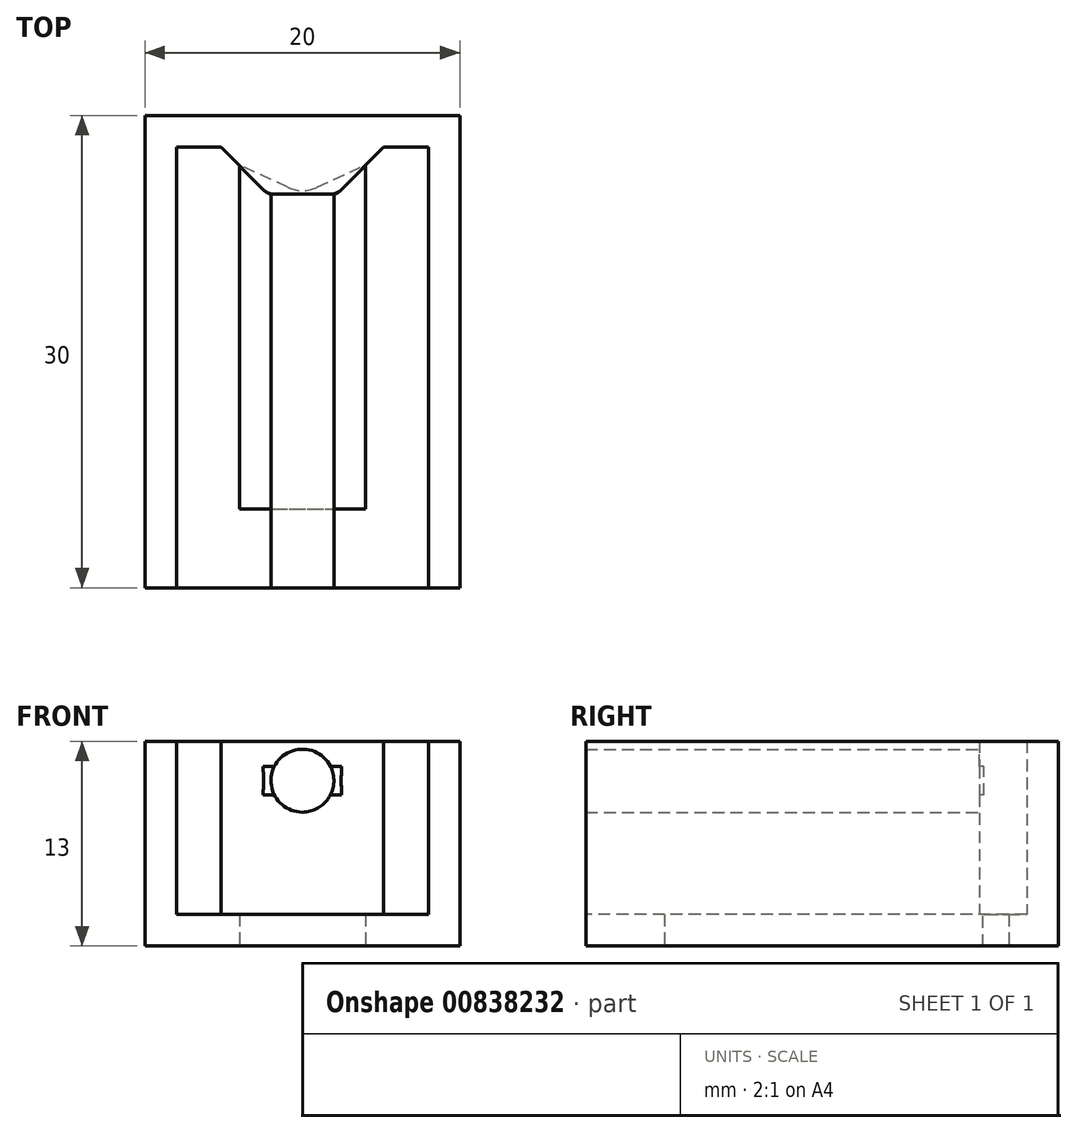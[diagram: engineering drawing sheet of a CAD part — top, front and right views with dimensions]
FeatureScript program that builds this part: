
annotation { "Feature Type Name" : "Feature", "Feature Type Description" : "" }
export const myFeature = defineFeature(function(context is Context, id is Id, definition is map)
    precondition{}
    {
        {
            var Q0;
            Q0=qCreatedBy(makeId("Top.planeOp"),FACE);
            var sketch = newSketch(context, id + "F0", { "sketchPlane" : qUnion([Q0])});
            skLineSegment(sketch, "E0.right", {"start": v(-10, 15) * mm, "end": v(-10, -15) * mm});
            skPoint(sketch, "E0.middle", {"position": v(0, 0) * mm});
            skLineSegment(sketch, "E1", {"start": v(0, 10) * mm, "end": v(-4, 11.86) * mm});
            skLineSegment(sketch, "E2.MirrorCS", {"start": v(10, 15) * mm, "end": v(10, -15) * mm});
            skLineSegment(sketch, "E3.MirrorCS", {"start": v(0, 10) * mm, "end": v(4, 11.86) * mm});
            skLineSegment(sketch, "E4.trimOffspring", {"start": v(-4, -10) * mm, "end": v(4, -10) * mm});
            skLineSegment(sketch, "E5", {"start": v(-4, 11.86) * mm, "end": v(-4, -10) * mm});
            skLineSegment(sketch, "E6", {"start": v(4, 11.86) * mm, "end": v(4, -10) * mm});
            skLineSegment(sketch, "E7", {"start": v(-10, -15) * mm, "end": v(10, -15) * mm});
            skLineSegment(sketch, "E8", {"start": v(-10, 15) * mm, "end": v(10, 15) * mm});
            skSolve(sketch);
        }
        {
            var Q0;
            Q0=makeQuery(id+"F0.imprint","IMPRINT",FACE,{"disambiguationData":[TD([[makeQuery(id+"F0.imprint","IMPRINT",EDGE,{"derivedFrom":sQuery(id+"F0.wireOp",EDGE,"E0.right")}),1.0]])]});
            extrude(context, id + "F1", {"entities" : qUnion([Q0]), "depth" : 2 * mm, "offsetDistance" : 25 * mm});
        }
        {
            var Q0;
            Q0=makeQuery(id+"F1.opExtrude","CAP_FACE",FACE,{"disambiguationData":[OSD([sQuery(id+"F0.wireOp",EDGE,"E0.right"),sQuery(id+"F0.wireOp",EDGE,"yTbLrUah-Ia5R-yqaf-Bvvm-QQtAT4T50mUZ"),sQuery(id+"F0.wireOp",EDGE,"NDNi7f39-i3bd-ZvMG-hIc7-ptrDR7INLeRJ"),sQuery(id+"F0.wireOp",EDGE,"E1"),sQuery(id+"F0.wireOp",EDGE,"E2.MirrorCS"),sQuery(id+"F0.wireOp",EDGE,"4e7f6cf4-dfac-4857-8eba-5604ad7142842.MirrorCS"),sQuery(id+"F0.wireOp",EDGE,"E3.MirrorCS"),sQuery(id+"F0.wireOp",EDGE,"4e7f6cf4-dfac-4857-8eba-5604ad7142845.MirrorCS"),sQuery(id+"F0.wireOp",EDGE,"E4.trimOffspring"),sQuery(id+"F0.wireOp",EDGE,"E5"),sQuery(id+"F0.wireOp",EDGE,"E6"),sQuery(id+"F0.wireOp",EDGE,"E7")])],"isStart":false});
            var sketch = newSketch(context, id + "F2", { "sketchPlane" : qUnion([Q0])});
            skLineSegment(sketch, "E9", {"start": v(0, 10) * mm, "end": v(-2.2, 10) * mm});
            skLineSegment(sketch, "E10", {"start": v(-2.2, 10) * mm, "end": v(-5.16, 13) * mm});
            skLineSegment(sketch, "E11", {"start": v(-5.16, 13) * mm, "end": v(-8, 13) * mm});
            skLineSegment(sketch, "E12", {"start": v(-8, 13) * mm, "end": v(-8, -15) * mm});
            skLineSegment(sketch, "E13", {"start": v(-8, -15) * mm, "end": v(-10, -15) * mm});
            skLineSegment(sketch, "E14", {"start": v(-10, -15) * mm, "end": v(-10, 15) * mm});
            skLineSegment(sketch, "E15.MirrorCS", {"start": v(0, 10) * mm, "end": v(2.2, 10) * mm});
            skLineSegment(sketch, "E16.MirrorCS", {"start": v(2.2, 10) * mm, "end": v(5.16, 13) * mm});
            skLineSegment(sketch, "E17.MirrorCS", {"start": v(5.16, 13) * mm, "end": v(8, 13) * mm});
            skLineSegment(sketch, "E18.MirrorCS", {"start": v(8, 13) * mm, "end": v(8, -15) * mm});
            skLineSegment(sketch, "E19.MirrorCS", {"start": v(8, -15) * mm, "end": v(10, -15) * mm});
            skLineSegment(sketch, "E20.MirrorCS", {"start": v(10, -15) * mm, "end": v(10, 15) * mm});
            skLineSegment(sketch, "E21", {"start": v(-10, 15) * mm, "end": v(10, 15) * mm});
            skSolve(sketch);
        }
        {
            var Q0;
            Q0 = qSketchRegion(id + "F2", true);
            extrude(context, id + "F3", {"entities" : qUnion([Q0]), "operationType" : NewBodyOperationType.ADD, "depth" : 11 * mm, "offsetDistance" : 25 * mm});
        }
        {
            var Q0;
            Q0=makeQuery(id+"F3.opExtrude","SWEPT_FACE",FACE,{"disambiguationData":[OSD([sQuery(id+"F2.wireOp",EDGE,"E9"),sQuery(id+"F2.wireOp",EDGE,"E15.MirrorCS")])]});
            var sketch = newSketch(context, id + "F4", { "sketchPlane" : qUnion([Q0])});
            skCircle(sketch, "E22", {"center": v(0, 10.5) * mm, "radius": 2 * mm});
            skPoint(sketch, "E22.centerSnap0", {"position": v(0, 13) * mm});
            skSolve(sketch);
        }
        {
            var Q0;
            Q0=makeQuery(id+"F4.imprint","IMPRINT",FACE,{"disambiguationData":[TD([[makeQuery(id+"F4.imprint","IMPRINT",EDGE,{"derivedFrom":sQuery(id+"F4.wireOp",EDGE,"E22")}),1.0]])]});
            extrude(context, id + "F5", {"entities" : qUnion([Q0]), "operationType" : NewBodyOperationType.ADD, "depth" : 25 * mm, "offsetDistance" : 25 * mm});
        }
        {
            var Q0;
            Q0=makeQuery(id+"F3.opExtrude","SWEPT_EDGE",EDGE,{"disambiguationData":[OSD([sQuery(id+"F2.wireOp",EDGE,"E15.MirrorCS"),sQuery(id+"F2.wireOp",EDGE,"E16.MirrorCS")])]});
            var Q1;
            Q1=makeQuery(id+"F3.opExtrude","SWEPT_EDGE",EDGE,{"disambiguationData":[OSD([sQuery(id+"F2.wireOp",EDGE,"E9"),sQuery(id+"F2.wireOp",EDGE,"E10")])]});
            fillet(context, id + "F6", {"entities" : qUnion([Q0, Q1]), "radius" : 1 * mm, "tangentPropagation" : true, "allowEdgeOverflow" : false});
        }
        {
            var Q0;
            Q0=makeQuery(id+"F1.opExtrude","SWEPT_EDGE",EDGE,{"disambiguationData":[OSD([sQuery(id+"F0.wireOp",EDGE,"E1"),sQuery(id+"F0.wireOp",EDGE,"E3.MirrorCS")])]});
            fillet(context, id + "F7", {"entities" : qUnion([Q0]), "radius" : 2.23 * mm, "tangentPropagation" : true, "allowEdgeOverflow" : false});
        }
        {
            var Q0;
            Q0=makeQuery(id+"F1.opExtrude","SWEPT_BODY",BODY,{"disambiguationData":[OSD([sQuery(id+"F0.wireOp",EDGE,"E0.right"),sQuery(id+"F0.wireOp",EDGE,"yTbLrUah-Ia5R-yqaf-Bvvm-QQtAT4T50mUZ"),sQuery(id+"F0.wireOp",EDGE,"NDNi7f39-i3bd-ZvMG-hIc7-ptrDR7INLeRJ"),sQuery(id+"F0.wireOp",EDGE,"E1"),sQuery(id+"F0.wireOp",EDGE,"E2.MirrorCS"),sQuery(id+"F0.wireOp",EDGE,"4e7f6cf4-dfac-4857-8eba-5604ad7142842.MirrorCS"),sQuery(id+"F0.wireOp",EDGE,"E3.MirrorCS"),sQuery(id+"F0.wireOp",EDGE,"4e7f6cf4-dfac-4857-8eba-5604ad7142845.MirrorCS"),sQuery(id+"F0.wireOp",EDGE,"E4.trimOffspring"),sQuery(id+"F0.wireOp",EDGE,"E5"),sQuery(id+"F0.wireOp",EDGE,"E6"),sQuery(id+"F0.wireOp",EDGE,"E7")])]});
            transform(context, id + "F8", {"entities" : qUnion([Q0]), "transformType" : TransformType.TRANSLATION_3D, "dx" : 43.7 * mm, "dy" : 0 * mm, "dz" : 0 * mm, "makeCopy" : true});
        }
        {
            var Q0;
            Q0=makeQuery(id+"F8.opPattern","COPY",BODY,{"derivedFrom":makeQuery(id+"F1.opExtrude","SWEPT_BODY",BODY,{"disambiguationData":[OSD([sQuery(id+"F0.wireOp",EDGE,"E0.right"),sQuery(id+"F0.wireOp",EDGE,"E1"),sQuery(id+"F0.wireOp",EDGE,"E2.MirrorCS"),sQuery(id+"F0.wireOp",EDGE,"E3.MirrorCS"),sQuery(id+"F0.wireOp",EDGE,"E4.trimOffspring"),sQuery(id+"F0.wireOp",EDGE,"E5"),sQuery(id+"F0.wireOp",EDGE,"E6"),sQuery(id+"F0.wireOp",EDGE,"E7"),sQuery(id+"F0.wireOp",EDGE,"E8")])]}),"instanceName":"1"});
            deleteBodies(context, id + "F9", {"entities" : qUnion([Q0])});
        }
    });
